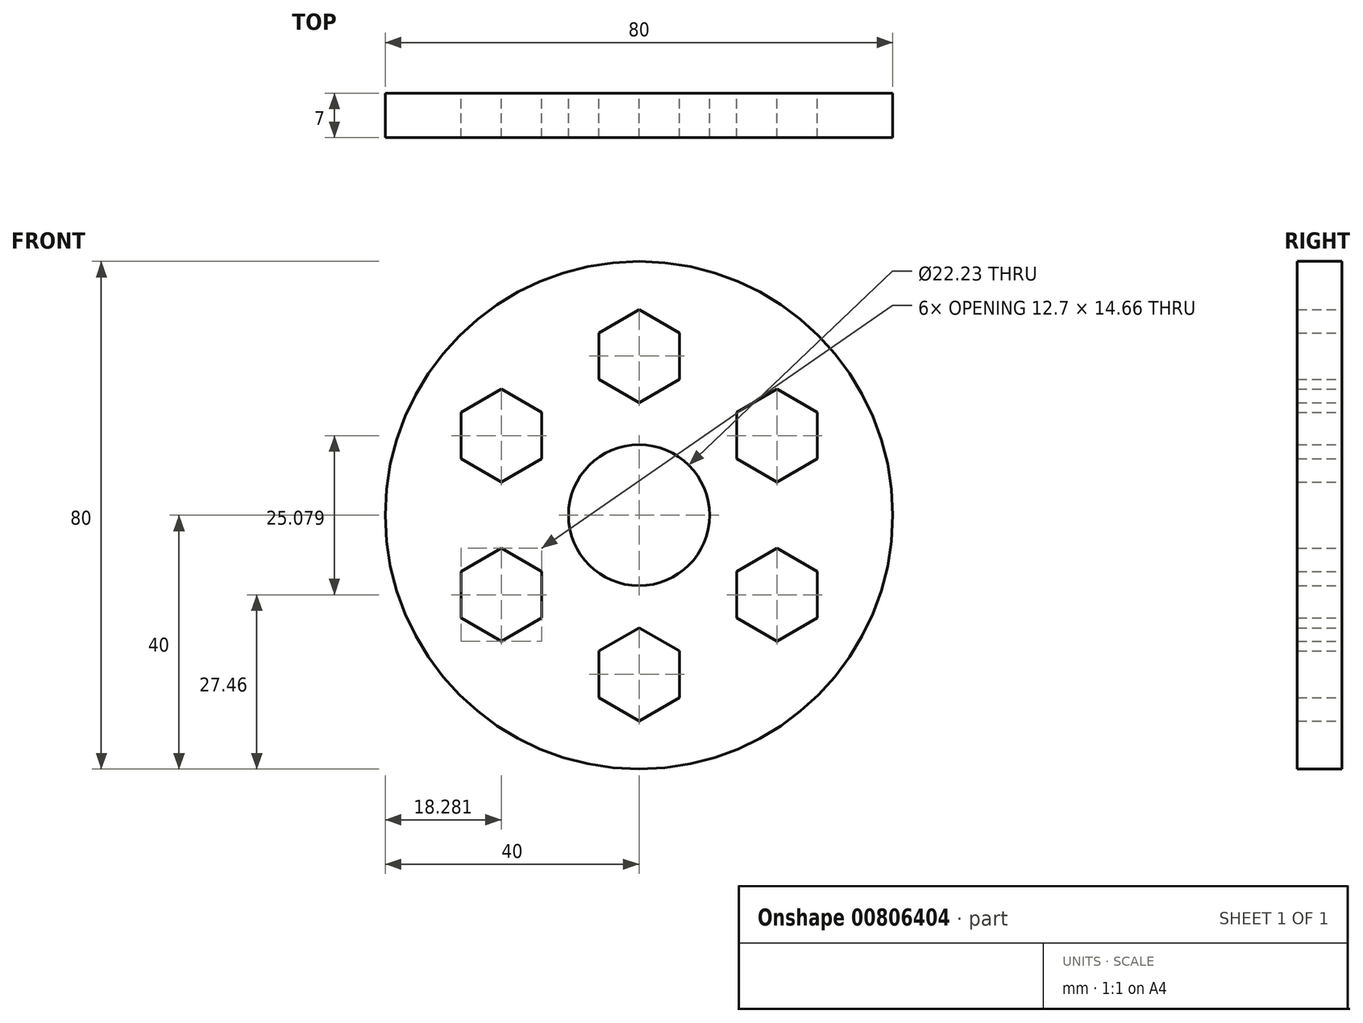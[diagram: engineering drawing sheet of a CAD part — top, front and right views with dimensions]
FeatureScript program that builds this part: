
annotation { "Feature Type Name" : "Feature", "Feature Type Description" : "" }
export const myFeature = defineFeature(function(context is Context, id is Id, definition is map)
    precondition{}
    {
        {
            var Q0;
            Q0=qCreatedBy(makeId("Front.planeOp"),FACE);
            var sketch = newSketch(context, id + "F0", { "sketchPlane" : qUnion([Q0])});
            skCircle(sketch, "E0", {"center": v(0, 0) * mm, "radius": 40 * mm});
            skCircle(sketch, "E1", {"center": v(0, 0) * mm, "radius": 11.11 * mm});
            skCircle(sketch, "E2.cCircle", {"center": v(0, 25.08) * mm, "radius": 7.33 * mm, "construction": true});
            skLineSegment(sketch, "E2.0", {"start": v(0, 17.75) * mm, "end": v(-6.35, 21.41) * mm});
            skLineSegment(sketch, "E2.1", {"start": v(-6.35, 21.41) * mm, "end": v(-6.35, 28.75) * mm});
            skLineSegment(sketch, "E2.2", {"start": v(-6.35, 28.75) * mm, "end": v(0, 32.41) * mm});
            skLineSegment(sketch, "E2.3", {"start": v(0, 32.41) * mm, "end": v(6.35, 28.75) * mm});
            skLineSegment(sketch, "E2.4", {"start": v(6.35, 28.75) * mm, "end": v(6.35, 21.41) * mm});
            skLineSegment(sketch, "E2.5", {"start": v(6.35, 21.41) * mm, "end": v(0, 17.75) * mm});
            skSolve(sketch);
        }
        {
            var Q0;
            Q0=makeQuery(id+"F0.imprint","IMPRINT",FACE,{"disambiguationData":[TD([[makeQuery(id+"F0.imprint","IMPRINT",EDGE,{"derivedFrom":sQuery(id+"F0.wireOp",EDGE,"E0")}),1.0]])]});
            extrude(context, id + "F1", {"entities" : qUnion([Q0]), "endBound" : BoundingType.SYMMETRIC, "depth" : 7 * mm, "offsetDistance" : 25 * mm});
        }
        {
            var Q0;
            Q0=makeQuery(id+"F1.opExtrude","SWEPT_FACE",FACE,{"disambiguationData":[OSD([sQuery(id+"F0.wireOp",EDGE,"E2.1")])]});
            var Q1;
            Q1=makeQuery(id+"F1.opExtrude","SWEPT_FACE",FACE,{"disambiguationData":[OSD([sQuery(id+"F0.wireOp",EDGE,"E2.0")])]});
            var Q2;
            Q2=makeQuery(id+"F1.opExtrude","SWEPT_FACE",FACE,{"disambiguationData":[OSD([sQuery(id+"F0.wireOp",EDGE,"E2.5")])]});
            var Q3;
            Q3=makeQuery(id+"F1.opExtrude","SWEPT_FACE",FACE,{"disambiguationData":[OSD([sQuery(id+"F0.wireOp",EDGE,"E2.3")])]});
            var Q4;
            Q4=makeQuery(id+"F1.opExtrude","SWEPT_FACE",FACE,{"disambiguationData":[OSD([sQuery(id+"F0.wireOp",EDGE,"E2.4")])]});
            var Q5;
            Q5=makeQuery(id+"F1.opExtrude","SWEPT_FACE",FACE,{"disambiguationData":[OSD([sQuery(id+"F0.wireOp",EDGE,"E2.2")])]});
            var Q6;
            Q6=makeQuery(id+"F1.opExtrude","CAP_EDGE",EDGE,{"disambiguationData":[OSD([sQuery(id+"F0.wireOp",EDGE,"E1")])],"isStart":false});
            circularPattern(context, id + "F2", {"patternType" : PatternType.FACE, "faces" : qUnion([Q0, Q1, Q2, Q3, Q4, Q5]), "axis" : qUnion([Q6]), "angle" : 360 * degree, "instanceCount" : 6, "equalSpace" : true});
        }
    });
